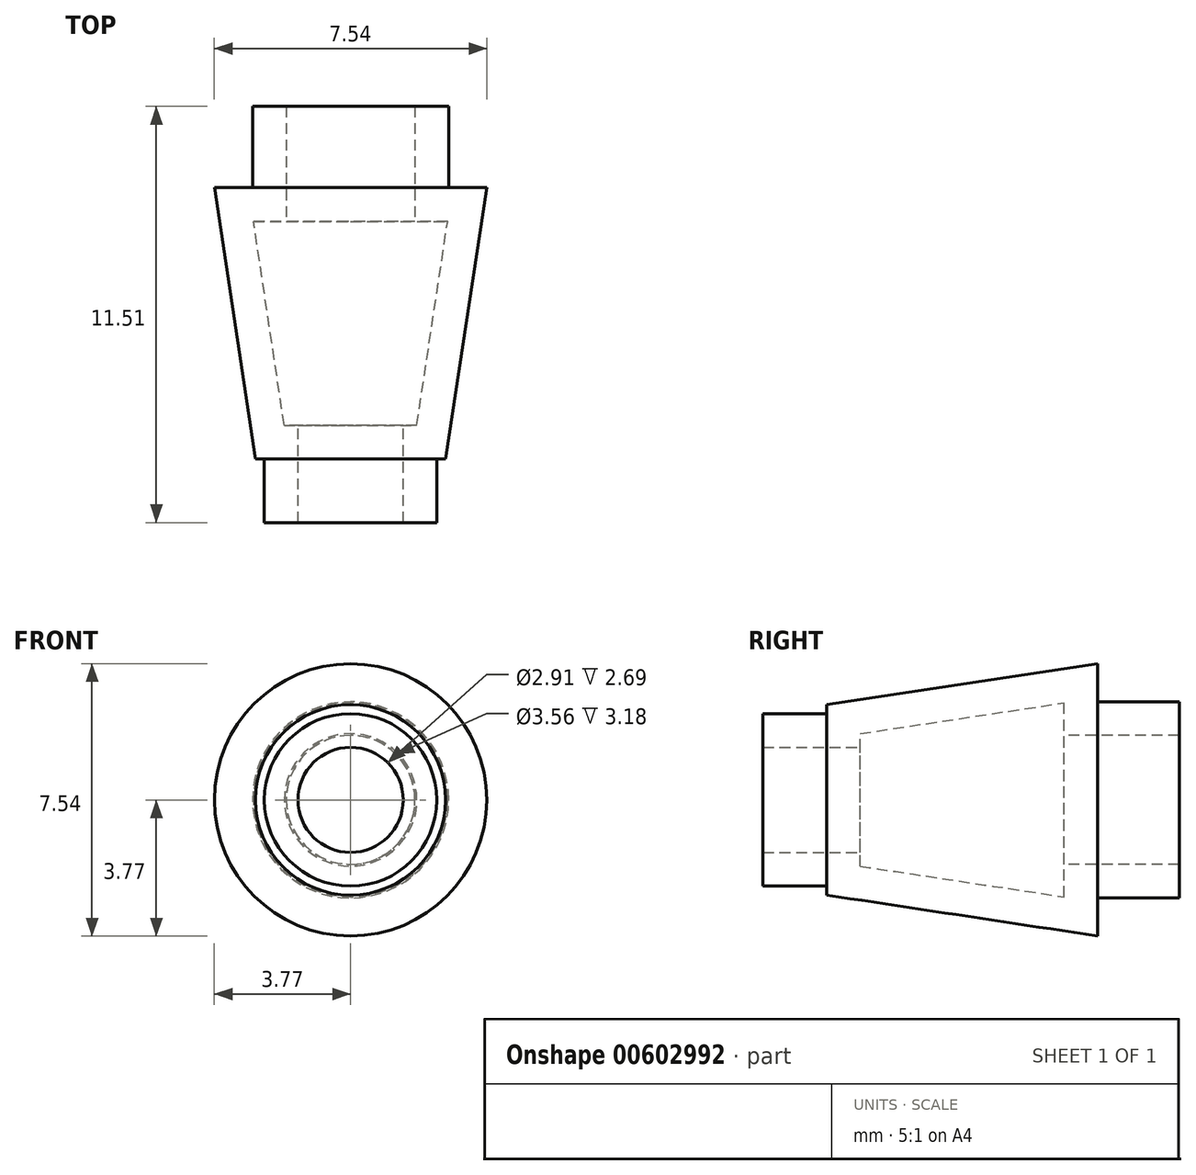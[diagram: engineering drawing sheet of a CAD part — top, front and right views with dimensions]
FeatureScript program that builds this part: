
annotation { "Feature Type Name" : "Feature", "Feature Type Description" : "" }
export const myFeature = defineFeature(function(context is Context, id is Id, definition is map)
    precondition{}
    {
        {
            var Q0;
            Q0=qCreatedBy(makeId("Front.planeOp"),FACE);
            var sketch = newSketch(context, id + "F0", { "sketchPlane" : qUnion([Q0])});
            skCircle(sketch, "E0", {"center": v(0, 0) * mm, "radius": 3.77 * mm});
            skSolve(sketch);
        }
        {
            var Q0;
            Q0 = qSketchRegion(id + "F0", true);
            extrude(context, id + "F1", {"entities" : qUnion([Q0]), "oppositeDirection" : true, "depth" : 7.5 * mm, "offsetDistance" : 25 * mm});
        }
        {
            var Q0;
            Q0=makeQuery(id+"F1.opExtrude","CAP_FACE",FACE,{"disambiguationData":[OSD([sQuery(id+"F0.wireOp",EDGE,"E0")])],"isStart":true});
            var sketch = newSketch(context, id + "F2", { "sketchPlane" : qUnion([Q0])});
            skCircle(sketch, "E1", {"center": v(0, 0) * mm, "radius": 2.63 * mm});
            skSolve(sketch);
        }
        {
            var Q1;
            Q1=makeQuery(id+"F1.opExtrude","CAP_FACE",FACE,{"disambiguationData":[OSD([sQuery(id+"F0.wireOp",EDGE,"E0")])],"isStart":false});
            var Q2;
            Q2=makeQuery(id+"F2.imprint","IMPRINT",FACE,{"disambiguationData":[TD([[makeQuery(id+"F2.imprint","IMPRINT",EDGE,{"derivedFrom":sQuery(id+"F2.wireOp",EDGE,"E1")}),1.0]])]});
            loft(context, id + "F3", {"operationType" : NewBodyOperationType.INTERSECT, "sheetProfilesArray" : [{ "sheetProfileEntities" : qUnion([Q1]) }, { "sheetProfileEntities" : qUnion([Q2]) }]});
        }
        {
            var Q0;
            Q0=qCreatedBy(makeId("Front.planeOp"),FACE);
            var sketch = newSketch(context, id + "F4", { "sketchPlane" : qUnion([Q0])});
            skCircle(sketch, "E2", {"center": v(0, 0) * mm, "radius": 2.39 * mm});
            skSolve(sketch);
        }
        {
            var Q0;
            Q0 = qSketchRegion(id + "F4", true);
            extrude(context, id + "F5", {"entities" : qUnion([Q0]), "operationType" : NewBodyOperationType.ADD, "depth" : 1.76 * mm, "offsetDistance" : 25 * mm});
        }
        {
            var Q0;
            Q0=makeQuery(id+"F1.opExtrude","CAP_FACE",FACE,{"disambiguationData":[OSD([sQuery(id+"F0.wireOp",EDGE,"E0")])],"isStart":false});
            var sketch = newSketch(context, id + "F6", { "sketchPlane" : qUnion([Q0])});
            skCircle(sketch, "E3", {"center": v(0, 0) * mm, "radius": 2.71 * mm});
            skSolve(sketch);
        }
        {
            var Q0;
            Q0=makeQuery(id+"F6.imprint","IMPRINT",FACE,{"disambiguationData":[TD([[makeQuery(id+"F6.imprint","IMPRINT",EDGE,{"derivedFrom":sQuery(id+"F6.wireOp",EDGE,"E3")}),1.0]])]});
            extrude(context, id + "F7", {"entities" : qUnion([Q0]), "operationType" : NewBodyOperationType.ADD, "depth" : 2.25 * mm, "offsetDistance" : 25 * mm});
        }
        {
            var Q0;
            Q0=makeQuery(id+"F5.opExtrude","CAP_FACE",FACE,{"disambiguationData":[OSD([sQuery(id+"F4.wireOp",EDGE,"E2")])],"isStart":false});
            var Q1;
            Q1=makeQuery(id+"F7.opExtrude","CAP_FACE",FACE,{"disambiguationData":[OSD([sQuery(id+"F6.wireOp",EDGE,"E3")])],"isStart":false});
            shell(context, id + "F8", {"entities" : qUnion([Q0, Q1]), "thickness" : 0.93 * mm});
        }
    });
